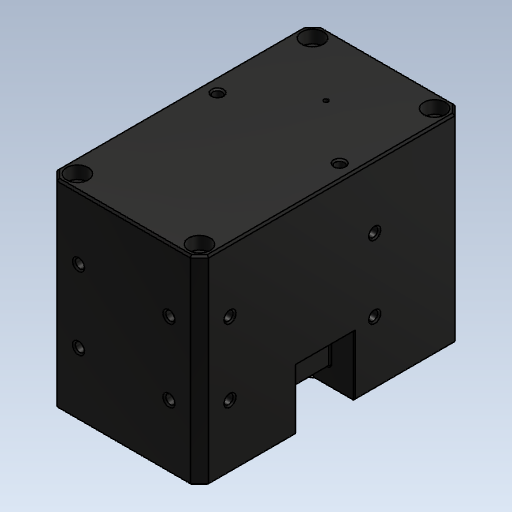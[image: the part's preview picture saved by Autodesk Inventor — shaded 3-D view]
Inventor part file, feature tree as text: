
AUTODESK INVENTOR PART (.ipt)
format: ipt  version: 2023 (Build 270158000, 158)  size: 420,352 bytes
history: native  units: mm
features: extrude x4, sketch x4, other x2, imported_body x1
ambient origin geometry x8: Origin, YZ Plane, XZ Plane, XY Plane, X Axis, Y Axis, Z Axis, Center Point
bodies: Body1 (feature_tree)
feature tree (11):
  other  "ソリッド1"
  other  "作業平面1"
  extrude  "押し出し1"  Depth=1.0mm
  extrude  "押し出し2"  Depth=10.0mm TaperAngle=0.0deg
  extrude  "押し出し3"  Depth=10.0mm TaperAngle=0.0deg
  extrude  "押し出し4"  Depth=1.0mm
  sketch  "スケッチ1"
  sketch  "スケッチ2"
  sketch  "スケッチ3"
  sketch  "スケッチ4"
  imported_body  "Base1"
